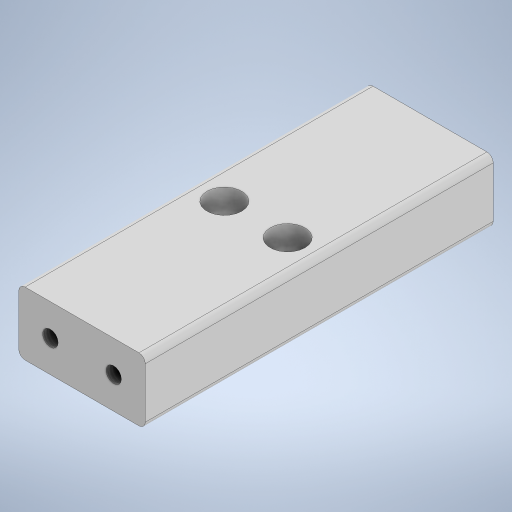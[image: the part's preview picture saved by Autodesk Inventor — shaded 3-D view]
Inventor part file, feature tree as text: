
AUTODESK INVENTOR PART (.ipt)
format: ipt  version: 2024.3 (Build 283343010, 343A)  size: 246,272 bytes
history: native  units: mm
features: sketch x4, hole x3, other x1, extrude x1, fillet x1, projected_geometry x1
ambient origin geometry x8: Origin, YZ Plane, XZ Plane, XY Plane, X Axis, Y Axis, Z Axis, Center Point
bodies: Body1 (feature_tree)
feature tree (11):
  other  "ソリッド1"
  extrude  "押し出し1"  Depth=20.0mm
  hole  "穴1"  [1 undecoded]
  hole  "穴2"  [1 undecoded]
  hole  "穴3"  [1 undecoded]
  fillet  "フィレット1"  Radius=5.0mm
  sketch  "スケッチ1"
  sketch  "スケッチ2"
  sketch  "スケッチ3"
  projected_geometry  "投影ループ1"
  sketch  "スケッチ5"
note: 3 required parameter values undecoded (feature->parameter linkage not recoverable at this tier; creation-order binding heuristic only, values carry confidence <= 0.55)
